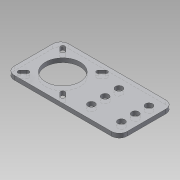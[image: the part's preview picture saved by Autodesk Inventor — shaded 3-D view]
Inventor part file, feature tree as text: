
AUTODESK INVENTOR PART (.ipt)
format: ipt  version: 2013 SP2 (Build 170200200, 200)  size: 162,304 bytes
history: native  units: mm
features: sketch x4, extrude x2, hole x2, plane x2, mirror x2, fillet x1
ambient origin geometry x8: Origin, YZ Plane, XZ Plane, XY Plane, X Axis, Y Axis, Z Axis, Center Point
bodies: Solid1 (feature_tree)
feature tree (13):
  extrude  "Extrusion1"  Depth=39.5mm
  hole  "Hole1"  [1 undecoded]
  extrude  "Extrusion2"  TaperAngle=45.0deg  [1 undecoded]
  plane  "Work Plane1"
  plane  "Work Plane2"
  mirror  "Mirror1"
  mirror  "Mirror2"
  hole  "Hole2"  [1 undecoded]
  fillet  "Fillet1"  Radius=35.25mm
  sketch  "Sketch1"  dims[d0=82.0mm d1=39.5mm]
  sketch  "Sketch2"  dims[d2=3.0mm d3=0.0mm d4=21.25mm]
  sketch  "Sketch3"  dims[d5=25.0mm d6=6.0mm d7=4.0mm d8=2.0mm d9=90.0deg d10=8.0mm d11=20.594885mm d13=45.0deg]
  sketch  "Sketch4"  dims[d14=5.75mm d15=8.25mm d16=35.25mm d17=32.75mm d18=3.1mm d19=3.1mm d20=3.0mm d21=0.0mm d22=52.0mm d23=10.9mm d24=10.0mm d25=8.2mm d26=9.75mm d27=21.8mm d28=30.75mm d29=5.1mm d30=6.0mm d31=4.0mm d32=2.0mm d33=90.0deg d34=8.0mm d35=20.594885mm d36=5.75mm]
note: 3 required parameter values undecoded (feature->parameter linkage not recoverable at this tier; creation-order binding heuristic only, values carry confidence <= 0.55)
